# Revit family: PlumFix_Sink_ABEY_Laundry_Single Bowl_Face Based
name_source: partatom
category: Plumbing Fixtures
revit_build: Autodesk Revit 2016 (Build: 20150220_1215(x64)
units: mm (PartAtom-declared; Revit-internal decimal feet)

## family parameters
Cut with Voids When Loaded = Yes
Host = Face
OmniClass Number = 23.45.05.14.14
OmniClass Title = Sinks/Lavatories
Part Type = Normal
Room Calculation Point = No
Round Connector Dimension = Use Diameter
Shared = No

## types (1)
- 470w x 450d x 250h
    Assembly Code = 0.00
    BodyMaterial = z_Abey_Stainless Steel
    CW Connection = Yes
    CWFU = 0
    Default Elevation = 0 mm  [stored 0 ft]
    Description = 45 Litre Laundry Tub - Stainless Steel
    HW Connection = Yes
    HWFU = 0
    Manufacturer = Abey Australia
    Manufacturer_Overall Depth = 450 mm  [stored 1.47638 ft]
    Manufacturer_Overall Height = 250 mm  [stored 0.82021 ft]
    Manufacturer_Overall Width = 470 mm  [stored 1.54199 ft]
    Manufacturer_Spec Code = LT120
    Manufacturer_URL__Product Specific = https://www.abey.com.au
    Model = LT120
    ModifiedIssue_ANZRS = 20190823 $
    Type Comments = 470x450mm
    URL = https://www.abey.com.au
    Vent Connection = No
    WFU = 0
    Waste Connection = No

note: [stored X ft] marks values corroborated as IEEE doubles in the binary element streams (Revit-internal decimal feet)

## geometry (parser evidence)
native form markers: Sweep x5
no freeform markers — native parametric forms only
